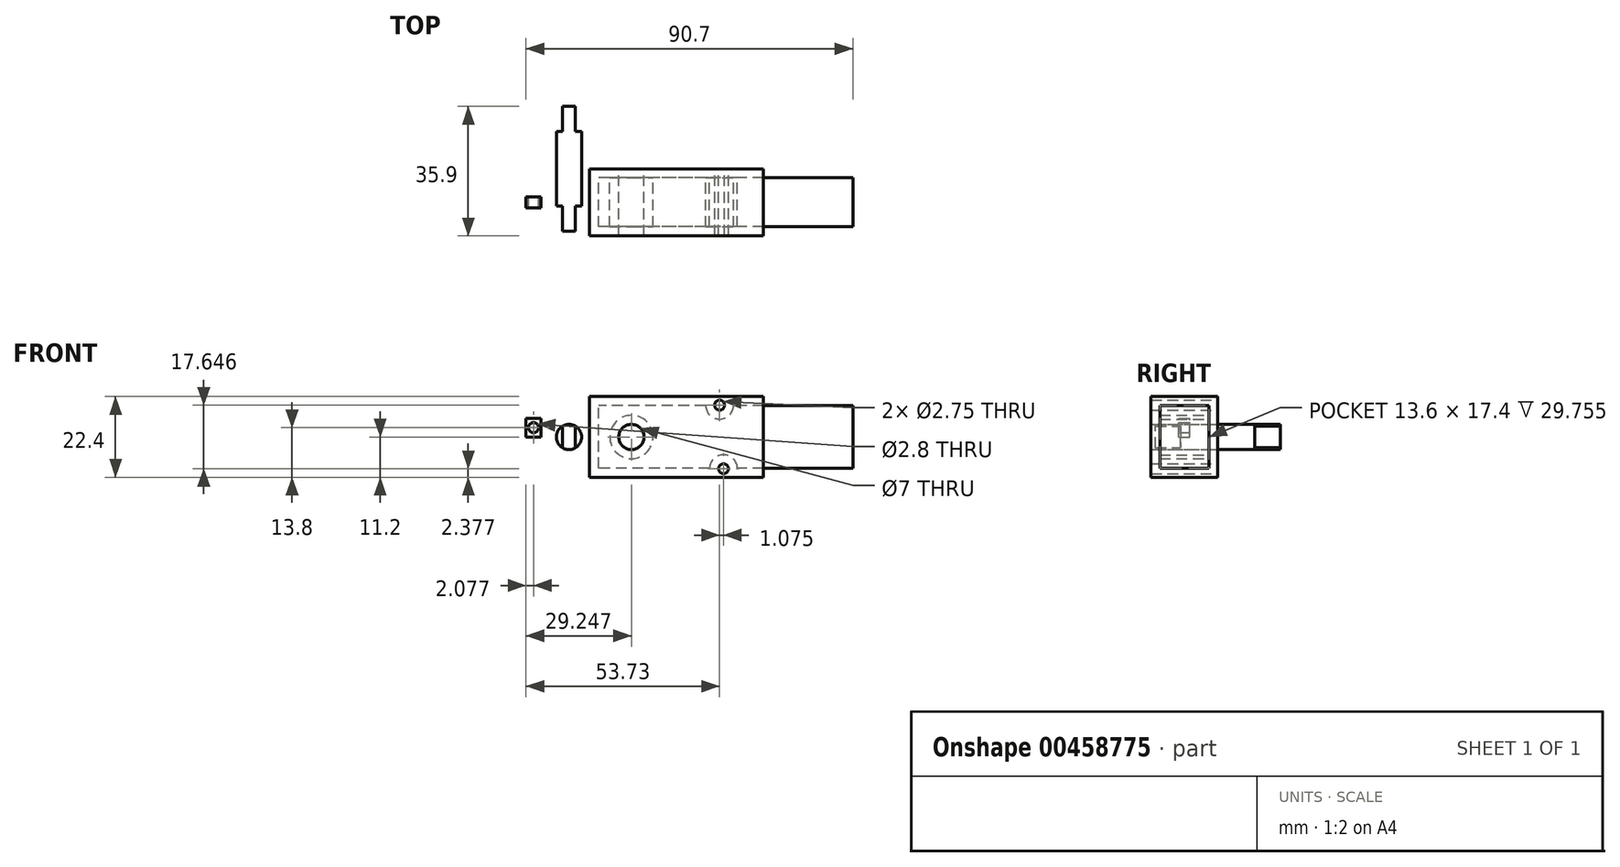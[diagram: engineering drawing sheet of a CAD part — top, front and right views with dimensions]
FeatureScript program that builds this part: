
annotation { "Feature Type Name" : "Feature", "Feature Type Description" : "" }
export const myFeature = defineFeature(function(context is Context, id is Id, definition is map)
    precondition{}
    {
        {
            var Q0;
            Q0=qCreatedBy(makeId("Front.planeOp"),FACE);
            var sketch = newSketch(context, id + "F0", { "sketchPlane" : qUnion([Q0])});
            skLineSegment(sketch, "E0.bottom", {"start": v(24.15, -11.2) * mm, "end": v(-24.15, -11.2) * mm});
            skLineSegment(sketch, "E0.top", {"start": v(24.15, 11.2) * mm, "end": v(-24.15, 11.2) * mm});
            skLineSegment(sketch, "E0.left", {"start": v(24.15, -11.2) * mm, "end": v(24.15, 11.2) * mm});
            skLineSegment(sketch, "E0.right", {"start": v(-24.15, -11.2) * mm, "end": v(-24.15, 11.2) * mm});
            skCircle(sketch, "E1", {"center": v(13.05, -8.82) * mm, "radius": 1.38 * mm});
            skCircle(sketch, "E2", {"center": v(11.98, 8.82) * mm, "radius": 1.38 * mm});
            skPoint(sketch, "E3.endSnap0", {"position": v(-24.15, 0) * mm});
            skCircle(sketch, "E4", {"center": v(-12.5, 0) * mm, "radius": 3.5 * mm});
            skSolve(sketch);
        }
        {
            var Q0;
            Q0=makeQuery(id+"F0.imprint","IMPRINT",FACE,{"disambiguationData":[TD([[makeQuery(id+"F0.imprint","IMPRINT",EDGE,{"derivedFrom":sQuery(id+"F0.wireOp",EDGE,"E0.bottom")}),-1.0]])]});
            extrude(context, id + "F1", {"entities" : qUnion([Q0]), "depth" : 18.6 * mm, "symmetric" : true});
        }
        {
            var Q0;
            Q0=makeQuery(id+"F0.imprint","IMPRINT",FACE,{"disambiguationData":[TD([[makeQuery(id+"F0.imprint","IMPRINT",EDGE,{"derivedFrom":sQuery(id+"F0.wireOp",EDGE,"E4")}),1.0]])]});
            var sketch = newSketch(context, id + "F2", { "sketchPlane" : qUnion([Q0])});
            skCircle(sketch, "E5", {"center": v(-29.83, 0) * mm, "radius": 3.5 * mm});
            skLineSegment(sketch, "E6.bottom", {"start": v(-31.63, -3) * mm, "end": v(-28.03, -3) * mm});
            skLineSegment(sketch, "E6.top", {"start": v(-31.63, 3) * mm, "end": v(-28.03, 3) * mm});
            skLineSegment(sketch, "E6.left", {"start": v(-31.63, -3) * mm, "end": v(-31.63, 3) * mm});
            skLineSegment(sketch, "E6.right", {"start": v(-28.03, -3) * mm, "end": v(-28.03, 3) * mm});
            skSolve(sketch);
        }
        {
            var Q0;
            {var subQ0=sQuery(id+"F2.wireOp",EDGE,"E6.left");Q0=makeQuery(id+"F2.imprint","IMPRINT",FACE,{"disambiguationData":[TD([[makeQuery(id+"F2.imprint","IMPRINT",EDGE,{"derivedFrom":subQ0}),1.0]])]});}
            var Q1;
            {var subQ0=sQuery(id+"F2.wireOp",EDGE,"E6.right");Q1=makeQuery(id+"F2.imprint","IMPRINT",FACE,{"disambiguationData":[TD([[makeQuery(id+"F2.imprint","IMPRINT",EDGE,{"derivedFrom":subQ0}),-1.0]])]});}
            extrude(context, id + "F3", {"entities" : qUnion([Q0, Q1]), "depth" : 1 * mm});
        }
        {
            var Q0;
            {var subQ0=sQuery(id+"F2.wireOp",EDGE,"E6.top");Q0=makeQuery(id+"F2.imprint","IMPRINT",FACE,{"disambiguationData":[TD([[makeQuery(id+"F2.imprint","IMPRINT",EDGE,{"derivedFrom":subQ0}),1.0]])]});}
            var Q1;
            Q1=makeQuery(id+"F2.imprint","IMPRINT",FACE,{"disambiguationData":[TD([[makeQuery(id+"F2.imprint","IMPRINT",EDGE,{"derivedFrom":sQuery(id+"F2.wireOp",EDGE,"E6.bottom")}),1.0]])]});
            var Q2;
            {var subQ0=sQuery(id+"F2.wireOp",EDGE,"E6.bottom");Q2=makeQuery(id+"F2.imprint","IMPRINT",FACE,{"disambiguationData":[TD([[makeQuery(id+"F2.imprint","IMPRINT",EDGE,{"derivedFrom":subQ0}),-1.0]])]});}
            extrude(context, id + "F4", {"entities" : qUnion([Q0, Q1, Q2]), "depth" : 8 * mm});
        }
        {
            var Q0;
            {var subQ0=sQuery(id+"F2.wireOp",EDGE,"E6.top");Q0=makeQuery(id+"F2.imprint","IMPRINT",FACE,{"disambiguationData":[TD([[makeQuery(id+"F2.imprint","IMPRINT",EDGE,{"derivedFrom":subQ0}),1.0]])]});}
            var sketch = newSketch(context, id + "F5", { "sketchPlane" : qUnion([Q0])});
            skCircle(sketch, "E7", {"center": v(-29.83, 0) * mm, "radius": 3.5 * mm});
            skSolve(sketch);
        }
        {
            var Q0;
            Q0 = qSketchRegion(id + "F5", true);
            extrude(context, id + "F6", {"entities" : qUnion([Q0]), "operationType" : NewBodyOperationType.ADD, "oppositeDirection" : true, "depth" : 18.6 * mm});
        }
        {
            var Q0;
            Q0=makeQuery(id+"F6.opExtrude","CAP_FACE",FACE,{"disambiguationData":[OSD([sQuery(id+"F5.wireOp",EDGE,"E7")])],"isStart":false});
            var sketch = newSketch(context, id + "F7", { "sketchPlane" : qUnion([Q0])});
            skLineSegment(sketch, "E8.bottom", {"start": v(31.63, -3) * mm, "end": v(28.03, -3) * mm});
            skLineSegment(sketch, "E8.top", {"start": v(31.63, 3) * mm, "end": v(28.03, 3) * mm});
            skLineSegment(sketch, "E8.left", {"start": v(31.63, -3) * mm, "end": v(31.63, 3) * mm});
            skLineSegment(sketch, "E8.right", {"start": v(28.03, -3) * mm, "end": v(28.03, 3) * mm});
            skPoint(sketch, "E8.middle", {"position": v(29.83, 0) * mm});
            skSolve(sketch);
        }
        {
            var Q0;
            {var subQ0=sQuery(id+"F7.wireOp",EDGE,"E8.left");Q0=makeQuery(id+"F7.imprint","IMPRINT",FACE,{"disambiguationData":[TD([[makeQuery(id+"F7.imprint","IMPRINT",EDGE,{"derivedFrom":subQ0}),-1.0]])]});}
            var Q1;
            {var subQ0=sQuery(id+"F7.wireOp",EDGE,"E8.right");Q1=makeQuery(id+"F7.imprint","IMPRINT",FACE,{"disambiguationData":[TD([[makeQuery(id+"F7.imprint","IMPRINT",EDGE,{"derivedFrom":subQ0}),1.0]])]});}
            extrude(context, id + "F8", {"entities" : qUnion([Q0, Q1]), "operationType" : NewBodyOperationType.ADD, "depth" : 1 * mm});
        }
        {
            var Q0;
            Q0=makeQuery(id+"F6.opExtrude","CAP_FACE",FACE,{"disambiguationData":[OSD([sQuery(id+"F5.wireOp",EDGE,"E7")])],"isStart":false});
            extrude(context, id + "F9", {"entities" : qUnion([Q0]), "operationType" : NewBodyOperationType.ADD, "depth" : 8 * mm});
        }
        {
            var Q0;
            Q0 = qSketchRegion(id + "F0", true);
            var sketch = newSketch(context, id + "F10", { "sketchPlane" : qUnion([Q0])});
            skLineSegment(sketch, "E9", {"start": v(-37.6, 0) * mm, "end": v(-37.6, 5.2) * mm});
            skLineSegment(sketch, "E10", {"start": v(-37.6, 5.2) * mm, "end": v(-41.75, 5.2) * mm});
            skLineSegment(sketch, "E11", {"start": v(-41.75, 5.2) * mm, "end": v(-41.75, 0) * mm});
            skLineSegment(sketch, "E12", {"start": v(-41.75, 0) * mm, "end": v(-37.6, 0) * mm});
            skCircle(sketch, "E13", {"center": v(-39.67, 2.6) * mm, "radius": 1.4 * mm});
            skPoint(sketch, "E13.centerSnap0", {"position": v(-41.75, 2.6) * mm});
            skPoint(sketch, "E13.centerSnap1", {"position": v(-39.67, 0) * mm});
            skSolve(sketch);
        }
        {
            var Q0;
            Q0 = qSketchRegion(id + "F10", true);
            extrude(context, id + "F11", {"entities" : qUnion([Q0]), "depth" : 3 * mm, "symmetric" : true});
        }
        {
            var Q0;
            Q0=makeQuery(id+"F1.opExtrude","SWEPT_FACE",FACE,{"disambiguationData":[OSD([sQuery(id+"F0.wireOp",EDGE,"E0.left")])]});
            shell(context, id + "F12", {"entities" : qUnion([Q0]), "thickness" : 2.5 * mm});
        }
        {
            var Q0;
            Q0=makeQuery(id+"F1.opExtrude","SWEPT_FACE",FACE,{"disambiguationData":[OSD([sQuery(id+"F0.wireOp",EDGE,"E0.left")])]});
            var sketch = newSketch(context, id + "F13", { "sketchPlane" : qUnion([Q0])});
            skLineSegment(sketch, "E14.bottom", {"start": v(6.8, -8.7) * mm, "end": v(-6.8, -8.7) * mm});
            skLineSegment(sketch, "E14.top", {"start": v(6.8, 8.7) * mm, "end": v(-6.8, 8.7) * mm});
            skLineSegment(sketch, "E14.left", {"start": v(6.8, -8.7) * mm, "end": v(6.8, 8.7) * mm});
            skLineSegment(sketch, "E14.right", {"start": v(-6.8, -8.7) * mm, "end": v(-6.8, 8.7) * mm});
            skPoint(sketch, "E14.middle", {"position": v(0, 0) * mm});
            skSolve(sketch);
        }
        {
            var Q0;
            Q0=makeQuery(id+"F13.imprint","IMPRINT",FACE,{"disambiguationData":[TD([[makeQuery(id+"F13.imprint","IMPRINT",EDGE,{"derivedFrom":sQuery(id+"F13.wireOp",EDGE,"E14.bottom")}),1.0]])]});
            extrude(context, id + "F14", {"entities" : qUnion([Q0]), "operationType" : NewBodyOperationType.ADD, "depth" : 24.8 * mm});
        }
    });
